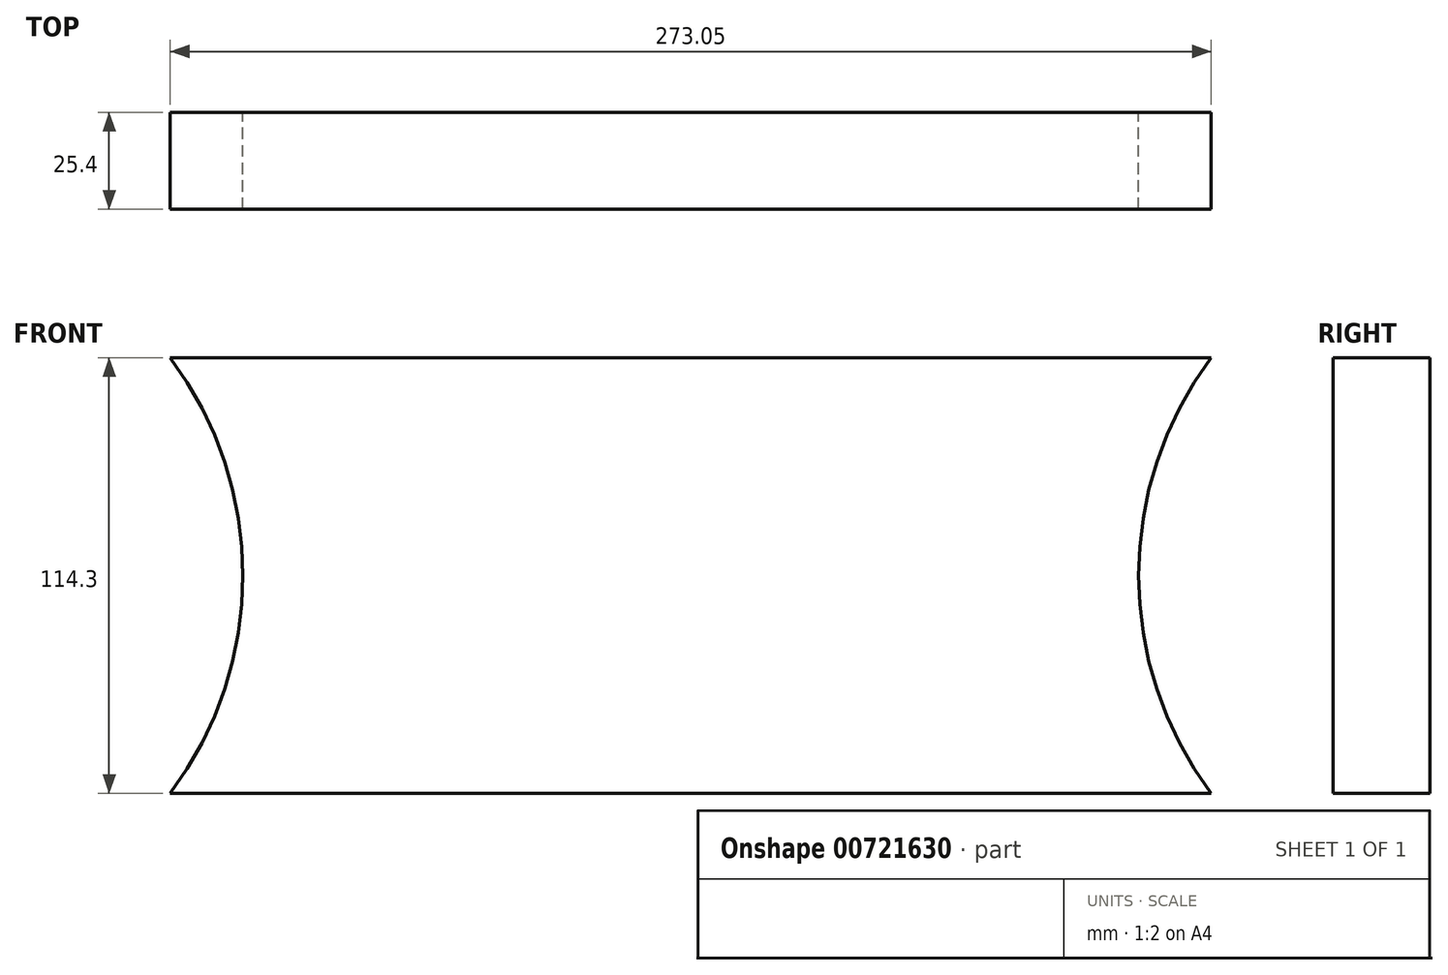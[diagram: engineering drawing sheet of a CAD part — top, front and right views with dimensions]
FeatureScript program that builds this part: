
annotation { "Feature Type Name" : "Feature", "Feature Type Description" : "" }
export const myFeature = defineFeature(function(context is Context, id is Id, definition is map)
    precondition{}
    {
        {
            var Q0;
            Q0=qCreatedBy(makeId("Front.planeOp"),FACE);
            var sketch = newSketch(context, id + "F0", { "sketchPlane" : qUnion([Q0])});
            skLineSegment(sketch, "E0.bottom", {"start": v(0, 0) * mm, "end": v(273.05, 0) * mm});
            skLineSegment(sketch, "E0.top", {"start": v(0, 114.3) * mm, "end": v(273.05, 114.3) * mm});
            skLineSegment(sketch, "E0.left", {"start": v(0, 0) * mm, "end": v(0, 114.3) * mm});
            skLineSegment(sketch, "E0.right", {"start": v(273.05, 0) * mm, "end": v(273.05, 114.3) * mm});
            skArc(sketch, "E1", {"start": v(0, 0) * mm, "mid": v(19.05, 57.15) * mm, "end": v(0, 114.3) * mm});
            skArc(sketch, "E2", {"start": v(273.05, 114.3) * mm, "mid": v(254, 57.15) * mm, "end": v(273.05, 0) * mm});
            skSolve(sketch);
        }
        {
            var Q0;
            Q0=makeQuery(id+"F0.imprint","IMPRINT",FACE,{"disambiguationData":[TD([[makeQuery(id+"F0.imprint","IMPRINT",EDGE,{"derivedFrom":sQuery(id+"F0.wireOp",EDGE,"E0.bottom")}),1.0]])]});
            extrude(context, id + "F1", {"entities" : qUnion([Q0]), "depth" : 25.4 * mm, "offsetDistance" : 25.4 * mm});
        }
    });
